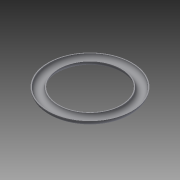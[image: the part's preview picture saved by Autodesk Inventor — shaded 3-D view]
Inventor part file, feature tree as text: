
AUTODESK INVENTOR PART (.ipt)
format: ipt  version: 2015 (Build 190159000, 159)  size: 128,512 bytes
history: native  units: in
note: dims shown in document units (in); Inventor stores cm internally (conversion verified against a paired STEP export)
features: sketch x2, revolve x1, extrude x1
ambient origin geometry x8: Origin, YZ Plane, XZ Plane, XY Plane, X Axis, Y Axis, Z Axis, Center Point
bodies: Body1 (feature_tree)
feature tree (4):
  revolve  "Revolution2"  [1 undecoded]
  extrude  "Extrusion2"  [1 undecoded]
  sketch  "Sketch3"  dims[d6=90.0deg d12=0.0in d13=0.0in]
  sketch  "Sketch5"
note: 2 required parameter values undecoded (feature->parameter linkage not recoverable at this tier; creation-order binding heuristic only, values carry confidence <= 0.55)